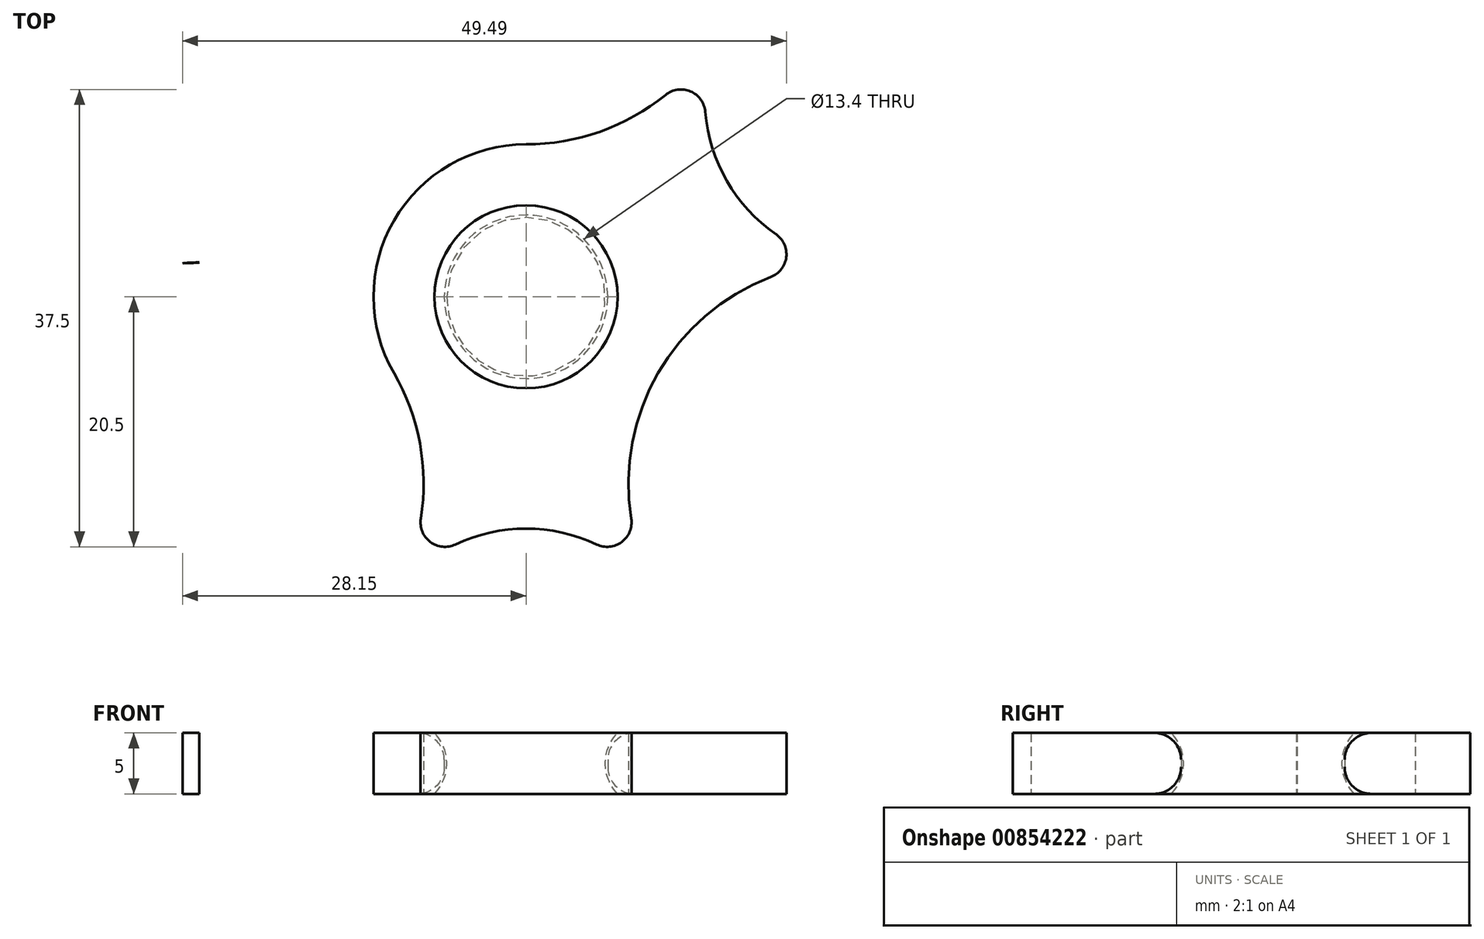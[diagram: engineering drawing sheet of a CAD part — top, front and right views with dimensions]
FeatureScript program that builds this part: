
annotation { "Feature Type Name" : "Feature", "Feature Type Description" : "" }
export const myFeature = defineFeature(function(context is Context, id is Id, definition is map)
    precondition{}
    {
        {
            var Q0;
            Q0=qCreatedBy(makeId("Top.planeOp"),FACE);
            var sketch = newSketch(context, id + "F0", { "sketchPlane" : qUnion([Q0])});
            skLineSegment(sketch, "E0", {"start": v(-19.93, 0) * mm, "end": v(17.22, 0) * mm, "construction": true});
            skLineSegment(sketch, "E1", {"start": v(0, 16.8) * mm, "end": v(0, -15.81) * mm, "construction": true});
            skCircle(sketch, "E2", {"center": v(0, 0) * mm, "radius": 6.5 * mm});
            skCircle(sketch, "E3.0", {"center": v(0, 0) * mm, "radius": 6.7 * mm});
            skCircle(sketch, "E4", {"center": v(0, 0) * mm, "radius": 7.5 * mm});
            skLineSegment(sketch, "E5", {"start": v(18.4, 10.62) * mm, "end": v(0, 0) * mm, "construction": true});
            skLineSegment(sketch, "E6", {"start": v(0, 0) * mm, "end": v(-28.15, 16.25) * mm, "construction": true});
            skLineSegment(sketch, "E7", {"start": v(0, 0) * mm, "end": v(0, -32.5) * mm, "construction": true});
            skLineSegment(sketch, "E8.MirrorCS", {"start": v(0, 0) * mm, "end": v(28.15, 16.25) * mm, "construction": true});
            skCircle(sketch, "E9", {"center": v(28.15, 16.25) * mm, "radius": 6.5 * mm});
            skCircle(sketch, "E10.0", {"center": v(28.15, 16.25) * mm, "radius": 6.7 * mm});
            skCircle(sketch, "E11", {"center": v(28.15, 16.25) * mm, "radius": 7.5 * mm});
            skCircle(sketch, "E12.MirrorC", {"center": v(-28.15, 16.25) * mm, "radius": 6.5 * mm});
            skCircle(sketch, "E13.MirrorC", {"center": v(-28.15, 16.25) * mm, "radius": 6.7 * mm});
            skCircle(sketch, "E14.MirrorC", {"center": v(-28.15, 16.25) * mm, "radius": 7.5 * mm});
            skCircle(sketch, "E15", {"center": v(0, -32.5) * mm, "radius": 6.5 * mm});
            skCircle(sketch, "E16.0", {"center": v(0, -32.5) * mm, "radius": 6.7 * mm});
            skCircle(sketch, "E17", {"center": v(0, -32.5) * mm, "radius": 7.5 * mm});
            skCircle(sketch, "E18.0", {"center": v(28.15, 16.25) * mm, "radius": 13.5 * mm});
            skCircle(sketch, "E19.MirrorC", {"center": v(-28.15, 16.25) * mm, "radius": 13.5 * mm});
            skCircle(sketch, "E20.0", {"center": v(0, 0) * mm, "radius": 12.5 * mm});
            skCircle(sketch, "E21.0", {"center": v(0, -32.5) * mm, "radius": 13.5 * mm});
            skPoint(sketch, "E22", {"position": v(0, 12.5) * mm});
            skLineSegment(sketch, "E23", {"start": v(0, 0) * mm, "end": v(-14.04, -8.1) * mm, "construction": true});
            skPoint(sketch, "E24", {"position": v(-10.83, -6.25) * mm});
            skLineSegment(sketch, "E25", {"start": v(0, 0) * mm, "end": v(13.38, -7.73) * mm, "construction": true});
            skPoint(sketch, "E26", {"position": v(10.83, -6.25) * mm});
            skLineSegment(sketch, "E27", {"start": v(-28.15, 16.25) * mm, "end": v(-21.4, 27.94) * mm, "construction": true});
            skLineSegment(sketch, "E28", {"start": v(-28.15, 16.25) * mm, "end": v(-34.9, 4.56) * mm, "construction": true});
            skLineSegment(sketch, "E29", {"start": v(28.15, 16.25) * mm, "end": v(21.4, 27.94) * mm, "construction": true});
            skLineSegment(sketch, "E30", {"start": v(28.15, 16.25) * mm, "end": v(34.9, 4.56) * mm, "construction": true});
            skLineSegment(sketch, "E31", {"start": v(0, -32.5) * mm, "end": v(-13.5, -32.5) * mm, "construction": true});
            skLineSegment(sketch, "E32", {"start": v(0, -32.5) * mm, "end": v(13.5, -32.5) * mm, "construction": true});
            skLineSegment(sketch, "E33", {"start": v(-28.15, 16.25) * mm, "end": v(-28.15, 2.75) * mm, "construction": true});
            skLineSegment(sketch, "E34", {"start": v(0, -32.5) * mm, "end": v(-11.7, -25.75) * mm, "construction": true});
            skArc(sketch, "E35", {"start": v(-11.7, -25.75) * mm, "mid": v(-10.83, -6.25) * mm, "end": v(-28.15, 2.75) * mm});
            skLineSegment(sketch, "E36", {"start": v(28.15, 16.25) * mm, "end": v(16.45, 23) * mm, "construction": true});
            skLineSegment(sketch, "E37", {"start": v(0, -32.5) * mm, "end": v(11.7, -25.75) * mm, "construction": true});
            skLineSegment(sketch, "E38", {"start": v(28.15, 16.25) * mm, "end": v(28.15, 2.75) * mm, "construction": true});
            skArc(sketch, "E39", {"start": v(28.15, 2.75) * mm, "mid": v(10.83, -6.25) * mm, "end": v(11.7, -25.75) * mm});
            skLineSegment(sketch, "E40", {"start": v(-28.15, 16.25) * mm, "end": v(-16.45, 23) * mm, "construction": true});
            skArc(sketch, "E41", {"start": v(-16.45, 23) * mm, "mid": v(0, 12.5) * mm, "end": v(16.45, 23) * mm});
            skSolve(sketch);
        }
        {
            var Q0;
            Q0=makeQuery(id+"F0.imprint","IMPRINT",FACE,{"disambiguationData":[TD([[makeQuery(id+"F0.imprint","IMPRINT",EDGE,{"derivedFrom":sQuery(id+"F0.wireOp",EDGE,"E4")}),-1.0]])]});
            var Q1;
            {var subQ0=sQuery(id+"F0.wireOp",EDGE,"E35");var subQ1=sQuery(id+"F0.wireOp",EDGE,"E19.MirrorC");var subQ2=makeQuery(id+"F0.imprint","INTERSECT",VERTEX,{"derivedFrom":[subQ1,subQ0]});Q1=makeQuery(id+"F0.imprint","IMPRINT",FACE,{"disambiguationData":[TD([[makeQuery(id+"F0.imprint","IMPRINT",EDGE,{"disambiguationData":[TD([[subQ2,1.0]])],"derivedFrom":subQ1}),1.0]])]});}
            var Q2;
            {var subQ0=sQuery(id+"F0.wireOp",EDGE,"pzDYve7j-JugV-Zf6D-BFaI-0Ue6WHaWEBY3");var subQ1=sQuery(id+"F0.wireOp",EDGE,"E18.0");var subQ2=makeQuery(id+"F0.imprint","INTERSECT",VERTEX,{"derivedFrom":[subQ1,subQ0]});Q2=makeQuery(id+"F0.imprint","IMPRINT",FACE,{"disambiguationData":[TD([[makeQuery(id+"F0.imprint","IMPRINT",EDGE,{"disambiguationData":[TD([[subQ2,-1.0]])],"derivedFrom":subQ1}),-1.0]])]});}
            var Q3;
            {var subQ0=sQuery(id+"F0.wireOp",EDGE,"E35");var subQ1=sQuery(id+"F0.wireOp",EDGE,"E20.0");var subQ2=makeQuery(id+"F0.imprint","INTERSECT",VERTEX,{"derivedFrom":[subQ1,subQ0]});Q3=makeQuery(id+"F0.imprint","IMPRINT",FACE,{"disambiguationData":[TD([[makeQuery(id+"F0.imprint","IMPRINT",EDGE,{"disambiguationData":[TD([[subQ2,-1.0]])],"derivedFrom":subQ1}),-1.0]])]});}
            var Q4;
            Q4=makeQuery(id+"F0.imprint","IMPRINT",FACE,{"disambiguationData":[TD([[makeQuery(id+"F0.imprint","IMPRINT",EDGE,{"derivedFrom":sQuery(id+"F0.wireOp",EDGE,"E3.0")}),-1.0]])]});
            extrude(context, id + "F1", {"entities" : qUnion([Q0, Q1, Q2, Q3, Q4]), "depth" : 5 * mm, "offsetDistance" : 25 * mm});
        }
        {
            var Q0;
            Q0=makeQuery(id+"F1.opExtrude","SWEPT_EDGE",EDGE,{"disambiguationData":[OSD([sQuery(id+"F0.wireOp",EDGE,"E21.0"),sQuery(id+"F0.wireOp",EDGE,"E39")])]});
            var Q1;
            Q1=makeQuery(id+"F1.opExtrude","SWEPT_EDGE",EDGE,{"disambiguationData":[OSD([sQuery(id+"F0.wireOp",EDGE,"E21.0"),sQuery(id+"F0.wireOp",EDGE,"E35")])]});
            var Q2;
            Q2=makeQuery(id+"F1.opExtrude","SWEPT_EDGE",EDGE,{"disambiguationData":[OSD([sQuery(id+"F0.wireOp",EDGE,"E18.0"),sQuery(id+"F0.wireOp",EDGE,"E39")])]});
            var Q3;
            Q3=makeQuery(id+"F1.opExtrude","SWEPT_EDGE",EDGE,{"disambiguationData":[OSD([sQuery(id+"F0.wireOp",EDGE,"E18.0"),sQuery(id+"F0.wireOp",EDGE,"E41")])]});
            var Q4;
            Q4=makeQuery(id+"F1.opExtrude","SWEPT_EDGE",EDGE,{"disambiguationData":[OSD([sQuery(id+"F0.wireOp",EDGE,"E19.MirrorC"),sQuery(id+"F0.wireOp",EDGE,"E35")])]});
            var Q5;
            Q5=makeQuery(id+"F1.opExtrude","SWEPT_EDGE",EDGE,{"disambiguationData":[OSD([sQuery(id+"F0.wireOp",EDGE,"E19.MirrorC"),sQuery(id+"F0.wireOp",EDGE,"E41")])]});
            fillet(context, id + "F2", {"entities" : qUnion([Q0, Q1, Q2, Q3, Q4, Q5]), "radius" : 2 * mm, "tangentPropagation" : true, "allowEdgeOverflow" : false});
        }
        {
            var Q0;
            Q0=makeQuery(id+"F1.opExtrude","CAP_EDGE",EDGE,{"disambiguationData":[OSD([sQuery(id+"F0.wireOp",EDGE,"E4")])],"isStart":false});
            var Q1;
            Q1=makeQuery(id+"F1.opExtrude","CAP_EDGE",EDGE,{"disambiguationData":[OSD([sQuery(id+"F0.wireOp",EDGE,"E11")])],"isStart":false});
            var Q2;
            Q2=makeQuery(id+"F1.opExtrude","CAP_EDGE",EDGE,{"disambiguationData":[OSD([sQuery(id+"F0.wireOp",EDGE,"E17")])],"isStart":false});
            var Q3;
            Q3=makeQuery(id+"F1.opExtrude","CAP_EDGE",EDGE,{"disambiguationData":[OSD([sQuery(id+"F0.wireOp",EDGE,"E14.MirrorC")])],"isStart":false});
            var Q4;
            Q4=makeQuery(id+"F1.opExtrude","CAP_EDGE",EDGE,{"disambiguationData":[OSD([sQuery(id+"F0.wireOp",EDGE,"E14.MirrorC")])],"isStart":true});
            var Q5;
            Q5=makeQuery(id+"F1.opExtrude","CAP_EDGE",EDGE,{"disambiguationData":[OSD([sQuery(id+"F0.wireOp",EDGE,"E4")])],"isStart":true});
            var Q6;
            Q6=makeQuery(id+"F1.opExtrude","CAP_EDGE",EDGE,{"disambiguationData":[OSD([sQuery(id+"F0.wireOp",EDGE,"E17")])],"isStart":true});
            var Q7;
            Q7=makeQuery(id+"F1.opExtrude","CAP_EDGE",EDGE,{"disambiguationData":[OSD([sQuery(id+"F0.wireOp",EDGE,"E11")])],"isStart":true});
            var Q8;
            Q8=makeQuery(id+"F1.opExtrude","CAP_EDGE",EDGE,{"disambiguationData":[OSD([sQuery(id+"F0.wireOp",EDGE,"E3.0")])],"isStart":false});
            var Q9;
            Q9=makeQuery(id+"F1.opExtrude","CAP_EDGE",EDGE,{"disambiguationData":[OSD([sQuery(id+"F0.wireOp",EDGE,"E3.0")])],"isStart":true});
            fillet(context, id + "F3", {"entities" : qUnion([Q0, Q1, Q2, Q3, Q4, Q5, Q6, Q7, Q8, Q9]), "radius" : 2.2 * mm, "tangentPropagation" : true, "allowEdgeOverflow" : false});
        }
        {
            var Q0;
            Q0=qCreatedBy(makeId("Front.planeOp"),FACE);
            var sketch = newSketch(context, id + "F4", { "sketchPlane" : qUnion([Q0])});
            skLineSegment(sketch, "E42", {"start": v(0, 0) * mm, "end": v(0, 10.72) * mm, "construction": true});
            skPoint(sketch, "E43", {"position": v(0, 2.5) * mm});
            skPoint(sketch, "E44", {"position": v(0, 5) * mm});
            skLineSegment(sketch, "E45", {"start": v(0, 5) * mm, "end": v(7.5, 5) * mm});
            skLineSegment(sketch, "E46", {"start": v(0, 2.5) * mm, "end": v(6.5, 2.5) * mm, "construction": true});
            skLineSegment(sketch, "E47", {"start": v(0, 0) * mm, "end": v(7.5, 0) * mm});
            skArc(sketch, "E48", {"start": v(7.5, 5) * mm, "mid": v(6.5, 2.5) * mm, "end": v(7.5, 0) * mm});
            skLineSegment(sketch, "E49", {"start": v(0, 5) * mm, "end": v(0, 0) * mm});
            skSolve(sketch);
        }
        {
            var Q0;
            Q0=makeQuery(id+"F4.imprint","IMPRINT",FACE,{"disambiguationData":[TD([[makeQuery(id+"F4.imprint","IMPRINT",EDGE,{"derivedFrom":sQuery(id+"F4.wireOp",EDGE,"E45")}),-1.0]])]});
            var Q1;
            Q1=sQuery(id+"F4.wireOp",EDGE,"E42");
            revolve(context, id + "F5", {"surfaceOperationType" : NewSurfaceOperationType.NEW, "entities" : qUnion([Q0]), "axis" : qUnion([Q1]), "revolveType" : RevolveType.FULL});
        }
    });
